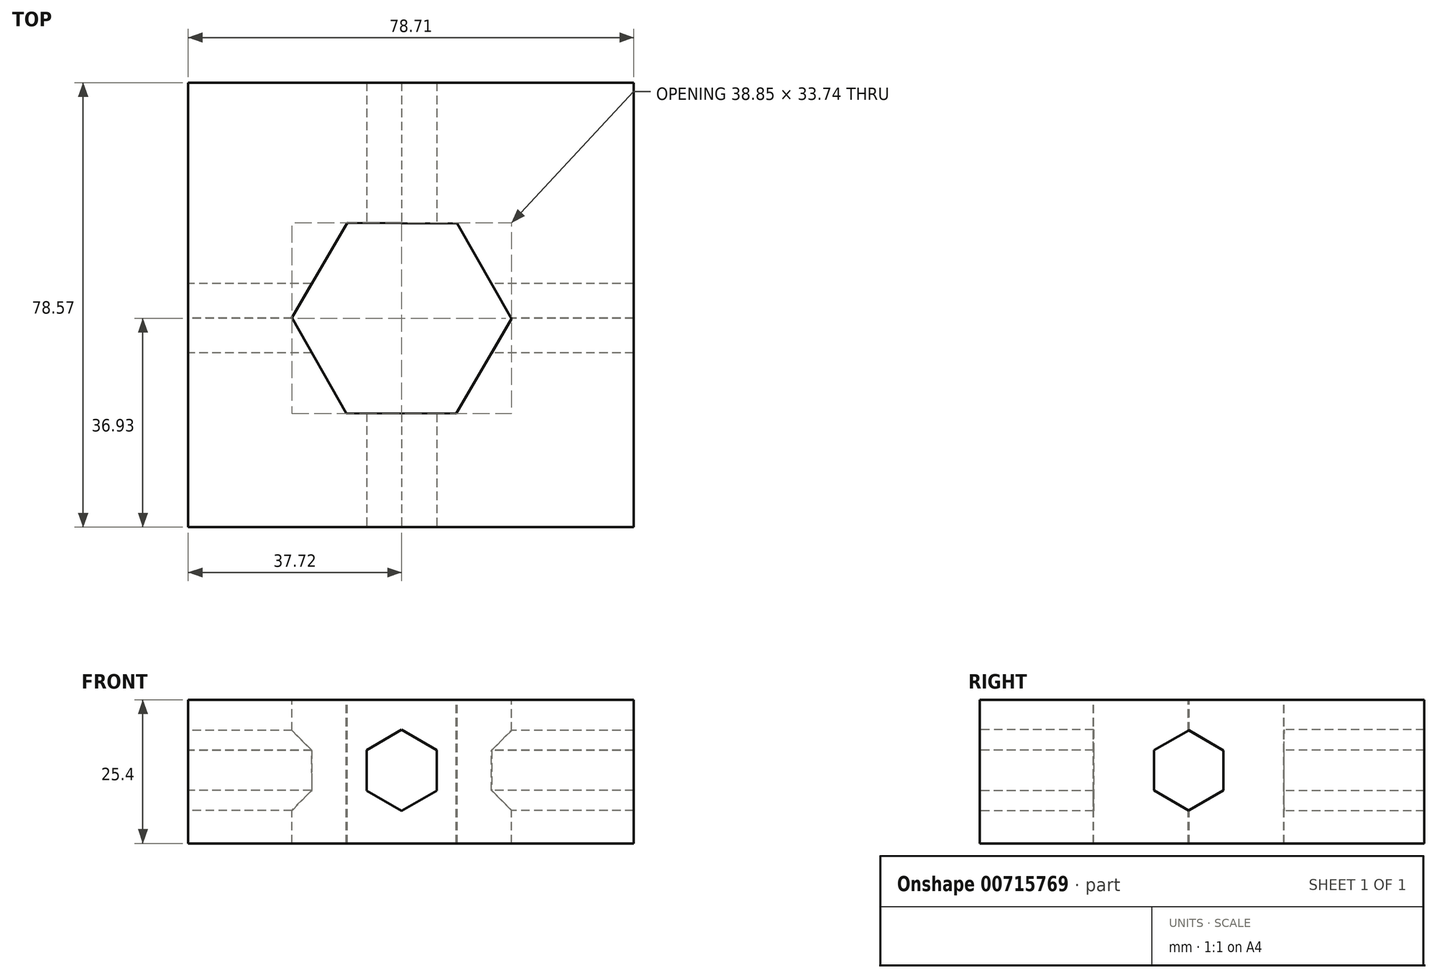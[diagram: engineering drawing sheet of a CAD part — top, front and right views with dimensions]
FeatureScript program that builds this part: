
annotation { "Feature Type Name" : "Feature", "Feature Type Description" : "" }
export const myFeature = defineFeature(function(context is Context, id is Id, definition is map)
    precondition{}
    {
        {
            var Q0;
            Q0=qCreatedBy(makeId("Top.planeOp"),FACE);
            var sketch = newSketch(context, id + "F0", { "sketchPlane" : qUnion([Q0])});
            skLineSegment(sketch, "E0.bottom", {"start": v(-37.72, -36.93) * mm, "end": v(41, -36.93) * mm});
            skLineSegment(sketch, "E0.top", {"start": v(-37.72, 41.64) * mm, "end": v(41, 41.64) * mm});
            skLineSegment(sketch, "E0.left", {"start": v(-37.72, -36.93) * mm, "end": v(-37.72, 41.64) * mm});
            skLineSegment(sketch, "E0.right", {"start": v(41, -36.93) * mm, "end": v(41, 41.64) * mm});
            skSolve(sketch);
        }
        {
            var Q0;
            Q0 = qSketchRegion(id + "F0", true);
            extrude(context, id + "F1", {"entities" : qUnion([Q0]), "depth" : 25.4 * mm, "offsetDistance" : 25.4 * mm});
        }
        {
            var Q0;
            Q0=makeQuery(id+"F1.opExtrude","CAP_FACE",FACE,{"disambiguationData":[OSD([sQuery(id+"F0.wireOp",EDGE,"E0.bottom"),sQuery(id+"F0.wireOp",EDGE,"E0.top"),sQuery(id+"F0.wireOp",EDGE,"E0.left"),sQuery(id+"F0.wireOp",EDGE,"E0.right")])],"isStart":false});
            var sketch = newSketch(context, id + "F2", { "sketchPlane" : qUnion([Q0])});
            skCircle(sketch, "E1.cCircle", {"center": v(0, 0) * mm, "radius": 16.82 * mm, "construction": true});
            skLineSegment(sketch, "E1.0", {"start": v(19.43, -0.1) * mm, "end": v(9.63, -16.87) * mm});
            skLineSegment(sketch, "E1.1", {"start": v(9.63, -16.87) * mm, "end": v(-9.8, -16.78) * mm});
            skLineSegment(sketch, "E1.2", {"start": v(-9.8, -16.78) * mm, "end": v(-19.43, 0.1) * mm});
            skLineSegment(sketch, "E1.3", {"start": v(-19.43, 0.1) * mm, "end": v(-9.63, 16.87) * mm});
            skLineSegment(sketch, "E1.4", {"start": v(-9.63, 16.87) * mm, "end": v(9.8, 16.78) * mm});
            skLineSegment(sketch, "E1.5", {"start": v(9.8, 16.78) * mm, "end": v(19.43, -0.1) * mm});
            skPoint(sketch, "E1.0.midPoint", {"position": v(14.53, -8.48) * mm});
            skSolve(sketch);
        }
        {
            var Q0;
            Q0=makeQuery(id+"F2.imprint","IMPRINT",FACE,{"disambiguationData":[TD([[makeQuery(id+"F2.imprint","IMPRINT",EDGE,{"derivedFrom":sQuery(id+"F2.wireOp",EDGE,"E1.0")}),-1.0]])]});
            extrude(context, id + "F3", {"entities" : qUnion([Q0]), "operationType" : NewBodyOperationType.REMOVE, "oppositeDirection" : true, "depth" : 25.4 * mm, "offsetDistance" : 25.4 * mm});
        }
        {
            var Q0;
            Q0=makeQuery(id+"F1.opExtrude","SWEPT_FACE",FACE,{"disambiguationData":[OSD([sQuery(id+"F0.wireOp",EDGE,"E0.left")])]});
            var sketch = newSketch(context, id + "F4", { "sketchPlane" : qUnion([Q0])});
            skCircle(sketch, "E2.cCircle", {"center": v(0, 12.9) * mm, "radius": 6.14 * mm, "construction": true});
            skLineSegment(sketch, "E2.0", {"start": v(-0.02, 20) * mm, "end": v(6.13, 16.47) * mm});
            skLineSegment(sketch, "E2.1", {"start": v(6.13, 16.47) * mm, "end": v(6.14, 9.38) * mm});
            skLineSegment(sketch, "E2.2", {"start": v(6.14, 9.38) * mm, "end": v(0.02, 5.82) * mm});
            skLineSegment(sketch, "E2.3", {"start": v(0.02, 5.82) * mm, "end": v(-6.13, 9.35) * mm});
            skLineSegment(sketch, "E2.4", {"start": v(-6.13, 9.35) * mm, "end": v(-6.14, 16.44) * mm});
            skLineSegment(sketch, "E2.5", {"start": v(-6.14, 16.44) * mm, "end": v(-0.02, 20) * mm});
            skPoint(sketch, "E2.0.midPoint", {"position": v(3.05, 18.23) * mm});
            skSolve(sketch);
        }
        {
            var Q0;
            Q0=makeQuery(id+"F4.imprint","IMPRINT",FACE,{"disambiguationData":[TD([[makeQuery(id+"F4.imprint","IMPRINT",EDGE,{"derivedFrom":sQuery(id+"F4.wireOp",EDGE,"E2.0")}),-1.0]])]});
            extrude(context, id + "F5", {"entities" : qUnion([Q0]), "operationType" : NewBodyOperationType.REMOVE, "endBound" : BoundingType.THROUGH_ALL, "oppositeDirection" : true, "depth" : mm, "offsetDistance" : 25.4 * mm});
        }
        {
            var Q0;
            Q0=makeQuery(id+"F1.opExtrude","SWEPT_FACE",FACE,{"disambiguationData":[OSD([sQuery(id+"F0.wireOp",EDGE,"E0.bottom")])]});
            var sketch = newSketch(context, id + "F6", { "sketchPlane" : qUnion([Q0])});
            skCircle(sketch, "E3.cCircle", {"center": v(0, 12.9) * mm, "radius": 6.2 * mm, "construction": true});
            skLineSegment(sketch, "E3.0", {"start": v(6.2, 16.5) * mm, "end": v(6.2, 9.32) * mm});
            skLineSegment(sketch, "E3.1", {"start": v(6.2, 9.32) * mm, "end": v(0, 5.74) * mm});
            skLineSegment(sketch, "E3.2", {"start": v(0, 5.74) * mm, "end": v(-6.2, 9.32) * mm});
            skLineSegment(sketch, "E3.3", {"start": v(-6.2, 9.32) * mm, "end": v(-6.2, 16.5) * mm});
            skLineSegment(sketch, "E3.4", {"start": v(-6.2, 16.5) * mm, "end": v(0, 20.08) * mm});
            skLineSegment(sketch, "E3.5", {"start": v(0, 20.08) * mm, "end": v(6.2, 16.5) * mm});
            skPoint(sketch, "E3.0.midPoint", {"position": v(6.2, 12.9) * mm});
            skSolve(sketch);
        }
        {
            var Q0;
            Q0 = qSketchRegion(id + "F6", true);
            extrude(context, id + "F7", {"entities" : qUnion([Q0]), "operationType" : NewBodyOperationType.REMOVE, "endBound" : BoundingType.THROUGH_ALL, "oppositeDirection" : true, "depth" : 25.4 * mm, "offsetDistance" : 25.4 * mm});
        }
    });
